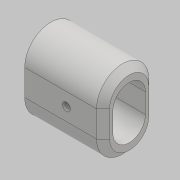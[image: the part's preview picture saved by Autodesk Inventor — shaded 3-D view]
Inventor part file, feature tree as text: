
AUTODESK INVENTOR PART (.ipt)
format: ipt  version: 2018 (Build 220112000, 112)  size: 123,392 bytes
history: native  units: mm
features: extrude x2, fillet x2, sketch x2, other x1, chamfer x1
ambient origin geometry x8: Origin, YZ Plane, XZ Plane, XY Plane, X Axis, Y Axis, Z Axis, Center Point
bodies: Body1 (feature_tree)
feature tree (8):
  other  "實體1"
  extrude  "擠出1"  Depth=40.0mm
  fillet  "圓角1"  Radius=60.0mm
  fillet  "圓角2"  Radius=25.0mm
  chamfer  "倒角1"  Distance=40.0mm
  extrude  "擠出2"  Depth=60.0mm TaperAngle=0.0deg
  sketch  "草圖1"
  sketch  "草圖2"
